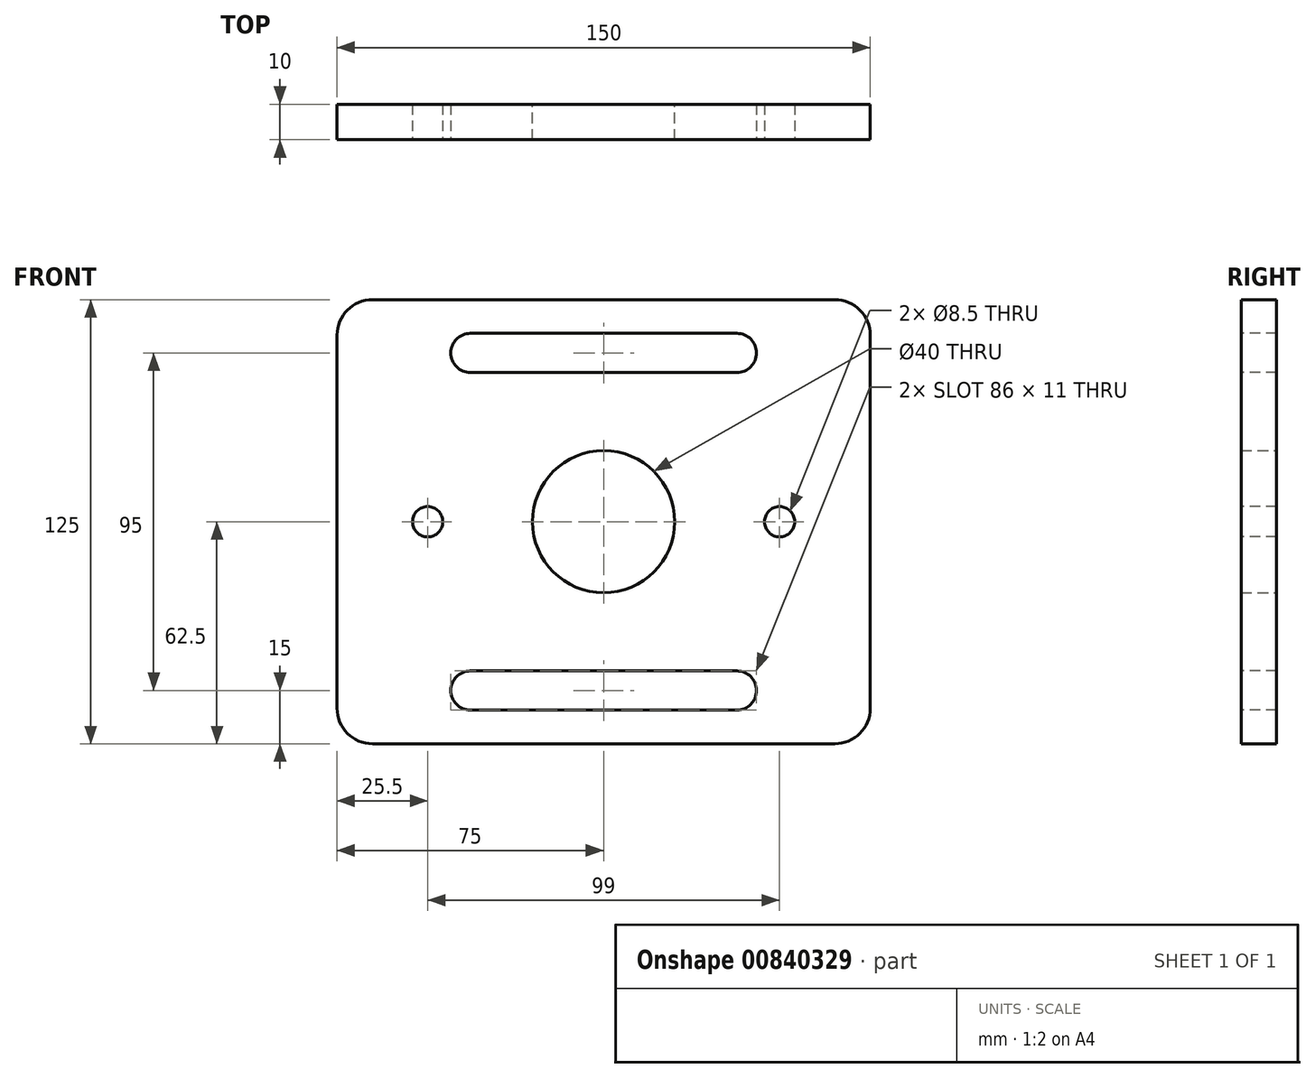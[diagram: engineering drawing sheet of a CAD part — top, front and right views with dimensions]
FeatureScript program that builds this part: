
annotation { "Feature Type Name" : "Feature", "Feature Type Description" : "" }
export const myFeature = defineFeature(function(context is Context, id is Id, definition is map)
    precondition{}
    {
        {
            var Q0;
            Q0=qCreatedBy(makeId("Front.planeOp"),FACE);
            var sketch = newSketch(context, id + "F0", { "sketchPlane" : qUnion([Q0])});
            skLineSegment(sketch, "E0.bottom", {"start": v(-75, 62.5) * mm, "end": v(75, 62.5) * mm});
            skLineSegment(sketch, "E0.top", {"start": v(-75, -62.5) * mm, "end": v(75, -62.5) * mm});
            skLineSegment(sketch, "E0.left", {"start": v(-75, 62.5) * mm, "end": v(-75, -62.5) * mm});
            skLineSegment(sketch, "E0.right", {"start": v(75, 62.5) * mm, "end": v(75, -62.5) * mm});
            skPoint(sketch, "E0.middle", {"position": v(0, 0) * mm});
            skCircle(sketch, "E1", {"center": v(0, 0) * mm, "radius": 20 * mm});
            skSolve(sketch);
        }
        {
            var Q0;
            Q0=qSketchRegion(id+"F0",true);
            extrude(context, id + "F1", {"entities" : qUnion([Q0]), "endBound" : BoundingType.SYMMETRIC, "depth" : 10 * mm, "offsetDistance" : 25 * mm});
        }
        {
            var Q0;
            Q0=makeQuery(id+"F1.opExtrude","SWEPT_EDGE",EDGE,{"disambiguationData":[OSD([sQuery(id+"F0.wireOp",EDGE,"E0.bottom"),sQuery(id+"F0.wireOp",EDGE,"E0.left")])]});
            var Q1;
            Q1=makeQuery(id+"F1.opExtrude","SWEPT_EDGE",EDGE,{"disambiguationData":[OSD([sQuery(id+"F0.wireOp",EDGE,"E0.bottom"),sQuery(id+"F0.wireOp",EDGE,"E0.right")])]});
            var Q2;
            Q2=makeQuery(id+"F1.opExtrude","SWEPT_EDGE",EDGE,{"disambiguationData":[OSD([sQuery(id+"F0.wireOp",EDGE,"E0.top"),sQuery(id+"F0.wireOp",EDGE,"E0.right")])]});
            var Q3;
            Q3=makeQuery(id+"F1.opExtrude","SWEPT_EDGE",EDGE,{"disambiguationData":[OSD([sQuery(id+"F0.wireOp",EDGE,"E0.top"),sQuery(id+"F0.wireOp",EDGE,"E0.left")])]});
            fillet(context, id + "F2", {"entities" : qUnion([Q0, Q1, Q2, Q3]), "radius" : 10 * mm, "tangentPropagation" : true, "allowEdgeOverflow" : false});
        }
        {
            var Q0;
            Q0=makeQuery(id+"F1.opExtrude","CAP_FACE",FACE,{"disambiguationData":[OSD([sQuery(id+"F0.wireOp",EDGE,"E0.bottom"),sQuery(id+"F0.wireOp",EDGE,"E0.top"),sQuery(id+"F0.wireOp",EDGE,"E0.left"),sQuery(id+"F0.wireOp",EDGE,"E0.right"),sQuery(id+"F0.wireOp",EDGE,"E1")])],"isStart":false});
            var sketch = newSketch(context, id + "F3", { "sketchPlane" : qUnion([Q0])});
            skPoint(sketch, "E2", {"position": v(-49.5, 0) * mm});
            skPoint(sketch, "E3", {"position": v(49.5, 0) * mm});
            skSolve(sketch);
        }
        {
            var Q0;
            Q0=sQuery(id+"F3.wireOp",VERTEX,"E2");
            var Q1;
            Q1=sQuery(id+"F3.wireOp",VERTEX,"E3");
            var Q2;
            Q2=makeQuery(id+"F1.opExtrude","SWEPT_BODY",BODY,{"disambiguationData":[OSD([sQuery(id+"F0.wireOp",EDGE,"E0.bottom"),sQuery(id+"F0.wireOp",EDGE,"E0.top"),sQuery(id+"F0.wireOp",EDGE,"E0.left"),sQuery(id+"F0.wireOp",EDGE,"E0.right"),sQuery(id+"F0.wireOp",EDGE,"E1")])]});
            hole(context, id + "F4", {"style" : HoleStyle.SIMPLE, "endStyle" : HoleEndStyle.BLIND, "standardTappedOrClearance" : lookupTablePath({ "standard" : "ISO", "engagement" : "75%", "pitch" : "1.5 mm", "size" : "M10", "type" : "Tapped" }), "standardBlindInLast" : lookupTablePath({ "standard" : "ISO", "engagement" : "75%", "pitch" : "1.5 mm", "size" : "M10", "type" : "Tapped" }), "holeDiameter" : 8.5 * mm, "majorDiameter" : 10 * mm, "showTappedDepth" : true, "holeDepth" : 24.5 * mm, "isTappedThrough" : true, "tappedDepth" : 20 * mm, "tapClearance" : 3, "startFromSketch" : true, "locations" : qUnion([Q0, Q1]), "scope" : qUnion([Q2])});
        }
        {
            var Q0;
            Q0=makeQuery(id+"F1.opExtrude","CAP_FACE",FACE,{"disambiguationData":[OSD([sQuery(id+"F0.wireOp",EDGE,"E0.bottom"),sQuery(id+"F0.wireOp",EDGE,"E0.top"),sQuery(id+"F0.wireOp",EDGE,"E0.left"),sQuery(id+"F0.wireOp",EDGE,"E0.right"),sQuery(id+"F0.wireOp",EDGE,"E1")])],"isStart":false});
            var sketch = newSketch(context, id + "F5", { "sketchPlane" : qUnion([Q0])});
            skLineSegment(sketch, "E4", {"start": v(-37.5, 47.5) * mm, "end": v(37.5, 47.5) * mm});
            skLineSegment(sketch, "E5", {"start": v(37.5, -47.5) * mm, "end": v(-37.5, -47.5) * mm});
            skLineSegment(sketch, "E6", {"start": v(0, 47.5) * mm, "end": v(0, -47.5) * mm, "construction": true});
            skArc(sketch, "E7.0.startCap", {"start": v(-37.5, 42) * mm, "mid": v(-43, 47.5) * mm, "end": v(-37.5, 53) * mm});
            skArc(sketch, "E7.0.endCap", {"start": v(37.5, 53) * mm, "mid": v(43, 47.5) * mm, "end": v(37.5, 42) * mm});
            skLineSegment(sketch, "E7.0.left", {"start": v(-37.5, 53) * mm, "end": v(37.5, 53) * mm});
            skLineSegment(sketch, "E7.0.right", {"start": v(-37.5, 42) * mm, "end": v(37.5, 42) * mm});
            skArc(sketch, "E7.1.startCap", {"start": v(37.5, -42) * mm, "mid": v(43, -47.5) * mm, "end": v(37.5, -53) * mm});
            skArc(sketch, "E7.1.endCap", {"start": v(-37.5, -53) * mm, "mid": v(-43, -47.5) * mm, "end": v(-37.5, -42) * mm});
            skLineSegment(sketch, "E7.1.left", {"start": v(37.5, -53) * mm, "end": v(-37.5, -53) * mm});
            skLineSegment(sketch, "E7.1.right", {"start": v(37.5, -42) * mm, "end": v(-37.5, -42) * mm});
            skSolve(sketch);
        }
        {
            var Q0;
            Q0 = qSketchRegion(id + "F5", true);
            extrude(context, id + "F6", {"entities" : qUnion([Q0]), "operationType" : NewBodyOperationType.REMOVE, "endBound" : BoundingType.THROUGH_ALL, "oppositeDirection" : true, "depth" : 25 * mm, "offsetDistance" : 25 * mm});
        }
    });
